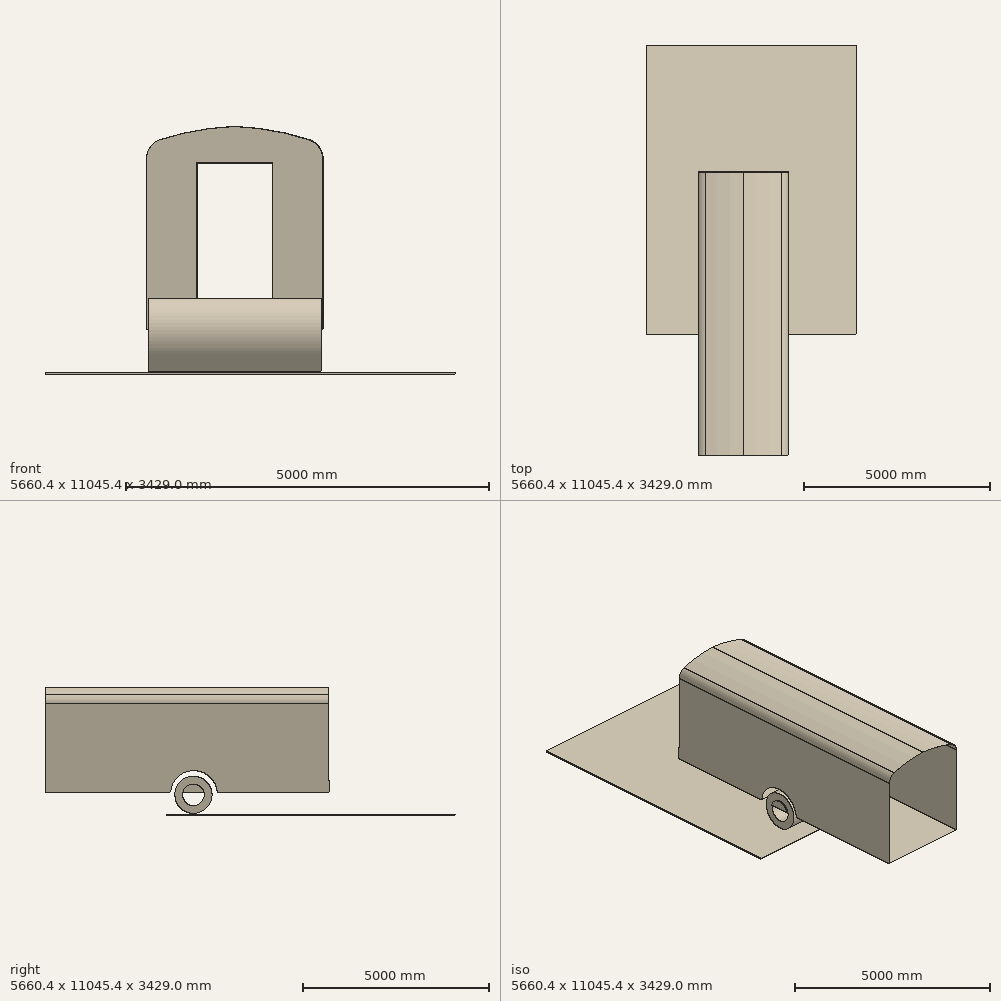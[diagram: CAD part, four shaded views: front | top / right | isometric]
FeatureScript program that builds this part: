
annotation { "Feature Type Name" : "Feature", "Feature Type Description" : "" }
export const myFeature = defineFeature(function(context is Context, id is Id, definition is map)
    precondition{}
    {
        {
            var Q0;
            Q0=qCreatedBy(makeId("Front.planeOp"),FACE);
            var sketch = newSketch(context, id + "F0", { "sketchPlane" : qUnion([Q0])});
            skLineSegment(sketch, "E0", {"start": v(0, 3516.26) * mm, "end": v(0, -3516.26) * mm, "construction": true});
            skLineSegment(sketch, "E1", {"start": v(0, 1879.6) * mm, "end": v(-520.7, 1879.6) * mm});
            skLineSegment(sketch, "E2", {"start": v(-520.7, 1879.6) * mm, "end": v(-520.7, 0) * mm});
            skLineSegment(sketch, "E3", {"start": v(-520.7, 0) * mm, "end": v(0, 0) * mm});
            skLineSegment(sketch, "E4", {"start": v(1241.73, -1016) * mm, "end": v(-3463.29, -1016) * mm});
            skLineSegment(sketch, "E5", {"start": v(1599.42, 2387.6) * mm, "end": v(-2922.17, 2387.6) * mm, "construction": true});
            skLineSegment(sketch, "E6", {"start": v(123.15, 1955.8) * mm, "end": v(-1219.2, 1955.8) * mm});
            skLineSegment(sketch, "E7", {"start": v(0, -114.3) * mm, "end": v(-1219.2, -114.3) * mm});
            skLineSegment(sketch, "E8", {"start": v(-1219.2, -114.3) * mm, "end": v(-1219.2, 1955.8) * mm});
            skArc(sketch, "E9", {"start": v(-1034.93, 2201.46) * mm, "mid": v(-1162.44, 2105.16) * mm, "end": v(-1219.2, 1955.8) * mm});
            skArc(sketch, "E10", {"start": v(0, 2387.6) * mm, "mid": v(-523.85, 2330) * mm, "end": v(-1034.93, 2201.46) * mm});
            skLineSegment(sketch, "E11", {"start": v(-1219.2, -114.3) * mm, "end": v(-1219.2, -419.1) * mm});
            skLineSegment(sketch, "E12", {"start": v(-1219.2, -419.1) * mm, "end": v(0, -419.1) * mm});
            skLineSegment(sketch, "E13.MirrorCS", {"start": v(-123.15, 1955.8) * mm, "end": v(1219.2, 1955.8) * mm});
            skLineSegment(sketch, "E14.MirrorCS", {"start": v(520.7, 0) * mm, "end": v(0, 0) * mm});
            skLineSegment(sketch, "E15.MirrorCS", {"start": v(0, -114.3) * mm, "end": v(1219.2, -114.3) * mm});
            skLineSegment(sketch, "E16.MirrorCS", {"start": v(1219.2, -114.3) * mm, "end": v(1219.2, 1955.8) * mm});
            skArc(sketch, "E17.MirrorCS", {"start": v(1034.93, 2201.46) * mm, "mid": v(1162.44, 2105.16) * mm, "end": v(1219.2, 1955.8) * mm});
            skArc(sketch, "E18.MirrorCS", {"start": v(0, 2387.6) * mm, "mid": v(523.85, 2330) * mm, "end": v(1034.93, 2201.46) * mm});
            skLineSegment(sketch, "E19.MirrorCS", {"start": v(1219.2, -114.3) * mm, "end": v(1219.2, -419.1) * mm});
            skLineSegment(sketch, "E20.MirrorCS", {"start": v(1219.2, -419.1) * mm, "end": v(0, -419.1) * mm});
            skLineSegment(sketch, "E21.MirrorCS", {"start": v(0, 1879.6) * mm, "end": v(520.7, 1879.6) * mm});
            skLineSegment(sketch, "E22.MirrorCS", {"start": v(520.7, 1879.6) * mm, "end": v(520.7, 0) * mm});
            skSolve(sketch);
        }
        {
            var Q0;
            Q0 = qSketchRegion(id + "F0", true);
            extrude(context, id + "F1", {"entities" : qUnion([Q0]), "depth" : 3.17 * mm});
        }
        {
            var Q0;
            Q0=makeQuery(id+"F1.opExtrude","CAP_FACE",FACE,{"disambiguationData":[OSD([sQuery(id+"F0.wireOp",EDGE,"E1"),sQuery(id+"F0.wireOp",EDGE,"E2"),sQuery(id+"F0.wireOp",EDGE,"E3"),sQuery(id+"F0.wireOp",EDGE,"E8"),sQuery(id+"F0.wireOp",EDGE,"E9"),sQuery(id+"F0.wireOp",EDGE,"E10"),sQuery(id+"F0.wireOp",EDGE,"E11"),sQuery(id+"F0.wireOp",EDGE,"E12"),sQuery(id+"F0.wireOp",EDGE,"E14.MirrorCS"),sQuery(id+"F0.wireOp",EDGE,"E16.MirrorCS"),sQuery(id+"F0.wireOp",EDGE,"E17.MirrorCS"),sQuery(id+"F0.wireOp",EDGE,"E18.MirrorCS"),sQuery(id+"F0.wireOp",EDGE,"E19.MirrorCS"),sQuery(id+"F0.wireOp",EDGE,"E20.MirrorCS"),sQuery(id+"F0.wireOp",EDGE,"E21.MirrorCS"),sQuery(id+"F0.wireOp",EDGE,"E22.MirrorCS")])],"isStart":false});
            var sketch = newSketch(context, id + "F2", { "sketchPlane" : qUnion([Q0])});
            skLineSegment(sketch, "E23.0", {"start": v(-1219.2, -419.1) * mm, "end": v(1219.2, -419.1) * mm});
            skLineSegment(sketch, "E24.0", {"start": v(-1219.2, 1955.8) * mm, "end": v(-1219.2, -419.1) * mm});
            skArc(sketch, "E25.0", {"start": v(-1034.93, 2201.46) * mm, "mid": v(-1162.44, 2105.16) * mm, "end": v(-1219.2, 1955.8) * mm});
            skArc(sketch, "E26.0", {"start": v(0, 2387.6) * mm, "mid": v(-523.85, 2330) * mm, "end": v(-1034.93, 2201.46) * mm});
            skArc(sketch, "E27.0", {"start": v(0, 2387.6) * mm, "mid": v(523.85, 2330) * mm, "end": v(1034.93, 2201.46) * mm});
            skArc(sketch, "E28.0", {"start": v(1034.93, 2201.46) * mm, "mid": v(1162.44, 2105.16) * mm, "end": v(1219.2, 1955.8) * mm});
            skLineSegment(sketch, "E29.0", {"start": v(1219.2, 1955.8) * mm, "end": v(1219.2, -419.1) * mm});
            skSolve(sketch);
        }
        {
            var Q0;
            Q0 = qSketchRegion(id + "F2", true);
            extrude(context, id + "F3", {"entities" : qUnion([Q0]), "operationType" : NewBodyOperationType.ADD, "depth" : 7620 * mm});
        }
        {
            var Q0;
            Q0=makeQuery(id+"F3.opExtrude","CAP_FACE",FACE,{"disambiguationData":[OSD([sQuery(id+"F2.wireOp",EDGE,"E23.0"),sQuery(id+"F2.wireOp",EDGE,"E24.0"),sQuery(id+"F2.wireOp",EDGE,"E25.0"),sQuery(id+"F2.wireOp",EDGE,"E26.0"),sQuery(id+"F2.wireOp",EDGE,"E27.0"),sQuery(id+"F2.wireOp",EDGE,"E28.0"),sQuery(id+"F2.wireOp",EDGE,"E29.0")])],"isStart":false});
            var Q1;
            Q1=makeQuery(id+"F3.opExtrude","CAP_FACE",FACE,{"disambiguationData":[OSD([sQuery(id+"F2.wireOp",EDGE,"E23.0"),sQuery(id+"F2.wireOp",EDGE,"E24.0"),sQuery(id+"F2.wireOp",EDGE,"E25.0"),sQuery(id+"F2.wireOp",EDGE,"E26.0"),sQuery(id+"F2.wireOp",EDGE,"E27.0"),sQuery(id+"F2.wireOp",EDGE,"E28.0"),sQuery(id+"F2.wireOp",EDGE,"E29.0")])],"isStart":true});
            var Q2;
            Q2=makeQuery(id+"F1.opExtrude","SWEPT_BODY",BODY,{"disambiguationData":[OSD([sQuery(id+"F0.wireOp",EDGE,"E1"),sQuery(id+"F0.wireOp",EDGE,"E2"),sQuery(id+"F0.wireOp",EDGE,"E3"),sQuery(id+"F0.wireOp",EDGE,"E8"),sQuery(id+"F0.wireOp",EDGE,"E9"),sQuery(id+"F0.wireOp",EDGE,"E10"),sQuery(id+"F0.wireOp",EDGE,"E11"),sQuery(id+"F0.wireOp",EDGE,"E12"),sQuery(id+"F0.wireOp",EDGE,"E14.MirrorCS"),sQuery(id+"F0.wireOp",EDGE,"E16.MirrorCS"),sQuery(id+"F0.wireOp",EDGE,"E17.MirrorCS"),sQuery(id+"F0.wireOp",EDGE,"E18.MirrorCS"),sQuery(id+"F0.wireOp",EDGE,"E19.MirrorCS"),sQuery(id+"F0.wireOp",EDGE,"E20.MirrorCS"),sQuery(id+"F0.wireOp",EDGE,"E21.MirrorCS"),sQuery(id+"F0.wireOp",EDGE,"E22.MirrorCS")])]});
            shell(context, id + "F4", {"entities" : qUnion([Q0, Q1]), "parts" : qUnion([Q2]), "thickness" : 2.54 * mm});
        }
        {
            var Q0;
            Q0=makeQuery(id+"F0.imprint","IMPRINT",FACE,{"disambiguationData":[TD([[makeQuery(id+"F0.imprint","IMPRINT",EDGE,{"derivedFrom":sQuery(id+"F0.wireOp",EDGE,"E7")}),1.0]])]});
            extrude(context, id + "F5", {"entities" : qUnion([Q0]), "operationType" : NewBodyOperationType.ADD, "oppositeDirection" : true, "depth" : 25.4 * mm});
        }
        {
            var Q0;
            Q0=qCreatedBy(makeId("Right.planeOp"),FACE);
            var sketch = newSketch(context, id + "F6", { "sketchPlane" : qUnion([Q0])});
            skCircle(sketch, "E30", {"center": v(-3636.9, -495.29) * mm, "radius": 290.1 * mm});
            skCircle(sketch, "E31", {"center": v(-3636.9, -495.29) * mm, "radius": 501.29 * mm});
            skArc(sketch, "E32", {"start": v(-2994.72, -483.54) * mm, "mid": v(-3610.39, 156.54) * mm, "end": v(-4250.47, -459.13) * mm});
            skLineSegment(sketch, "E33", {"start": v(-4250.47, -459.13) * mm, "end": v(-4137.03, -461.33) * mm});
            skLineSegment(sketch, "E34.trimOffspring", {"start": v(-3135.81, -480.8) * mm, "end": v(-2994.72, -483.54) * mm});
            skSolve(sketch);
        }
        {
            var Q0;
            Q0 = qSketchRegion(id + "F6", true);
            extrude(context, id + "F7", {"entities" : qUnion([Q0]), "operationType" : NewBodyOperationType.REMOVE, "endBound" : BoundingType.SYMMETRIC, "oppositeDirection" : true, "depth" : 2540 * mm});
        }
        {
            var Q0;
            Q0=makeQuery(id+"F6.imprint","IMPRINT",FACE,{"disambiguationData":[TD([[makeQuery(id+"F6.imprint","IMPRINT",EDGE,{"derivedFrom":sQuery(id+"F6.wireOp",EDGE,"E30")}),-1.0]])]});
            extrude(context, id + "F8", {"entities" : qUnion([Q0]), "operationType" : NewBodyOperationType.ADD, "endBound" : BoundingType.SYMMETRIC, "depth" : 2387.6 * mm});
        }
        {
            var Q0;
            Q0=makeQuery(id+"F0.imprint","IMPRINT",FACE,{"disambiguationData":[TD([[makeQuery(id+"F0.imprint","IMPRINT",EDGE,{"derivedFrom":sQuery(id+"F0.wireOp",EDGE,"E1")}),-1.0]])]});
            cPlane(context, id + "F9", {"entities" : qUnion([Q0]), "cplaneType" : CPlaneType.OFFSET, "offset" : 304.8 * mm, "oppositeDirection" : true, "width" : 152.4 * mm, "height" : 152.4 * mm});
        }
        {
            var Q0;
            Q0=qCreatedBy(makeId("Top.planeOp"),FACE);
            cPlane(context, id + "F10", {"entities" : qUnion([Q0]), "cplaneType" : CPlaneType.OFFSET, "offset" : 1016 * mm, "oppositeDirection" : true, "width" : 152.4 * mm, "height" : 152.4 * mm});
        }
        {
            var Q0;
            Q0=qCreatedBy(id+"F10.planeOp",FACE);
            var sketch = newSketch(context, id + "F11", { "sketchPlane" : qUnion([Q0])});
            skLineSegment(sketch, "E35.bottom", {"start": v(-2613.62, -4373.45) * mm, "end": v(3046.82, -4373.45) * mm});
            skLineSegment(sketch, "E35.top", {"start": v(-2613.62, 3422.17) * mm, "end": v(3046.82, 3422.17) * mm});
            skLineSegment(sketch, "E35.left", {"start": v(-2613.62, -4373.45) * mm, "end": v(-2613.62, 3422.17) * mm});
            skLineSegment(sketch, "E35.right", {"start": v(3046.82, -4373.45) * mm, "end": v(3046.82, 3422.17) * mm});
            skSolve(sketch);
        }
        {
            var Q0;
            Q0=makeQuery(id+"F11.imprint","IMPRINT",FACE,{"disambiguationData":[TD([[makeQuery(id+"F11.imprint","IMPRINT",EDGE,{"derivedFrom":sQuery(id+"F11.wireOp",EDGE,"E35.bottom")}),1.0]])]});
            extrude(context, id + "F12", {"entities" : qUnion([Q0]), "operationType" : NewBodyOperationType.ADD, "oppositeDirection" : true, "depth" : 25.4 * mm});
        }
    });
